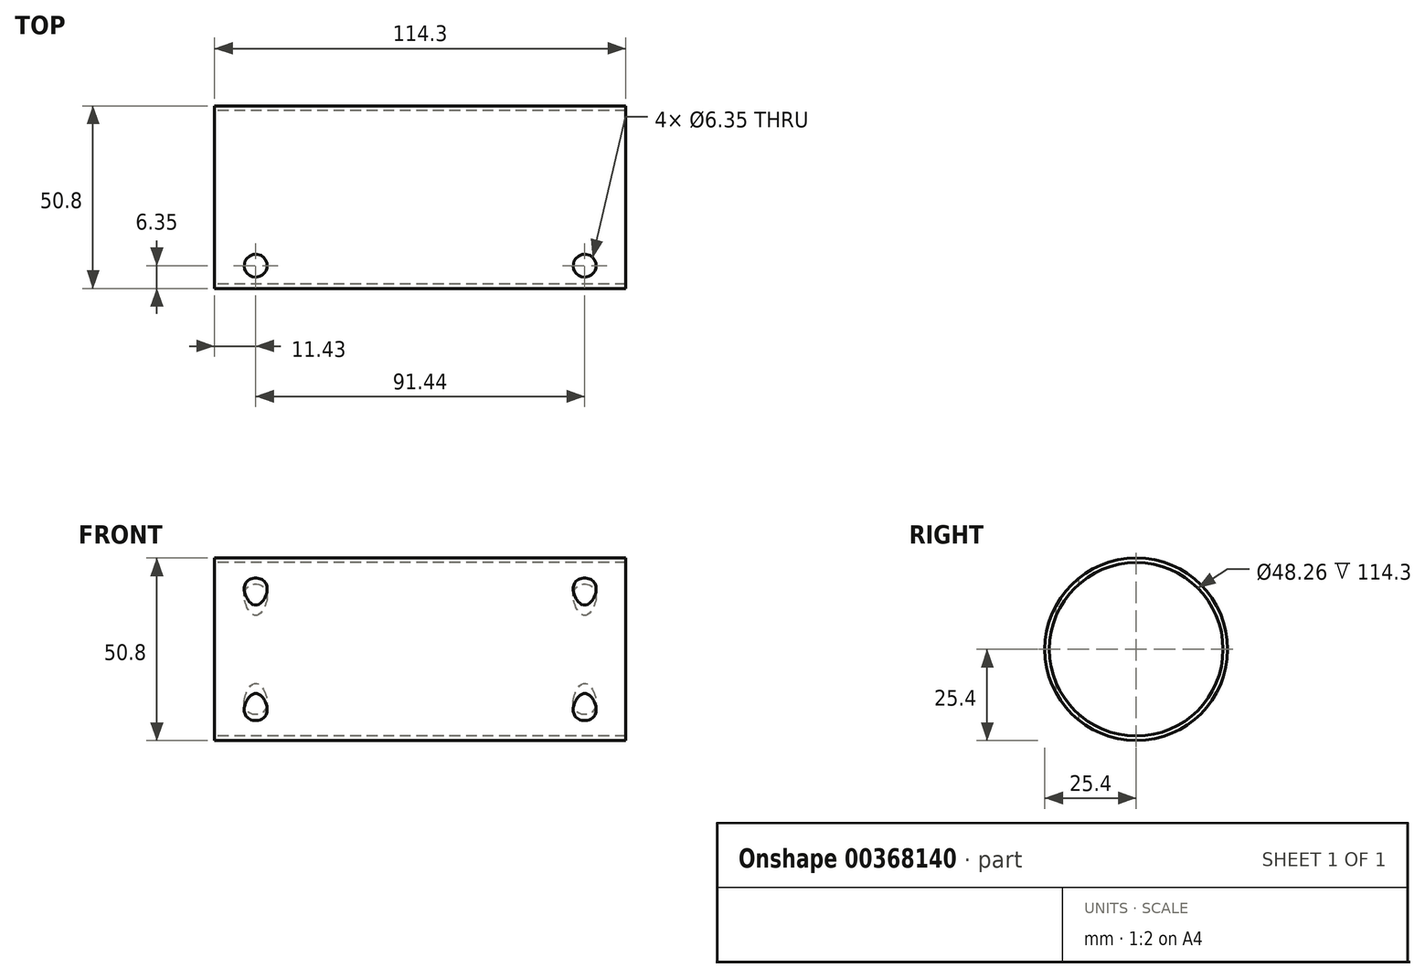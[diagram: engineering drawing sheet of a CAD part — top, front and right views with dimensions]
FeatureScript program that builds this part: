
annotation { "Feature Type Name" : "Feature", "Feature Type Description" : "" }
export const myFeature = defineFeature(function(context is Context, id is Id, definition is map)
    precondition{}
    {
        {
            var Q0;
            Q0=qCreatedBy(makeId("Right.planeOp"),FACE);
            var sketch = newSketch(context, id + "F0", { "sketchPlane" : qUnion([Q0])});
            skCircle(sketch, "E0", {"center": v(0, -25.4) * mm, "radius": 25.4 * mm});
            skCircle(sketch, "E1", {"center": v(0, -25.4) * mm, "radius": 24.13 * mm});
            skSolve(sketch);
        }
        {
            var Q0;
            Q0=makeQuery(id+"F0.imprint","IMPRINT",FACE,{"disambiguationData":[TD([[makeQuery(id+"F0.imprint","IMPRINT",EDGE,{"derivedFrom":sQuery(id+"F0.wireOp",EDGE,"E0")}),1.0]])]});
            extrude(context, id + "F1", {"entities" : qUnion([Q0]), "depth" : 114.3 * mm, "symmetric" : true});
        }
        {
            var Q0;
            Q0=qCreatedBy(makeId("Top.planeOp"),FACE);
            var sketch = newSketch(context, id + "F2", { "sketchPlane" : qUnion([Q0])});
            skLineSegment(sketch, "E2", {"start": v(0, 0) * mm, "end": v(45.72, 0) * mm});
            skLineSegment(sketch, "E3", {"start": v(45.72, 0) * mm, "end": v(45.72, -19.05) * mm});
            skLineSegment(sketch, "E4", {"start": v(0, 0) * mm, "end": v(-45.72, 0) * mm});
            skLineSegment(sketch, "E5", {"start": v(-45.72, 0) * mm, "end": v(-45.72, -19.05) * mm});
            skCircle(sketch, "E6", {"center": v(-45.72, -19.05) * mm, "radius": 3.18 * mm});
            skCircle(sketch, "E7", {"center": v(45.72, -19.05) * mm, "radius": 3.18 * mm});
            skSolve(sketch);
        }
        {
            var Q0;
            Q0 = qSketchRegion(id + "F2", true);
            extrude(context, id + "F3", {"entities" : qUnion([Q0]), "operationType" : NewBodyOperationType.REMOVE, "oppositeDirection" : true, "depth" : 50.8 * mm});
        }
    });
